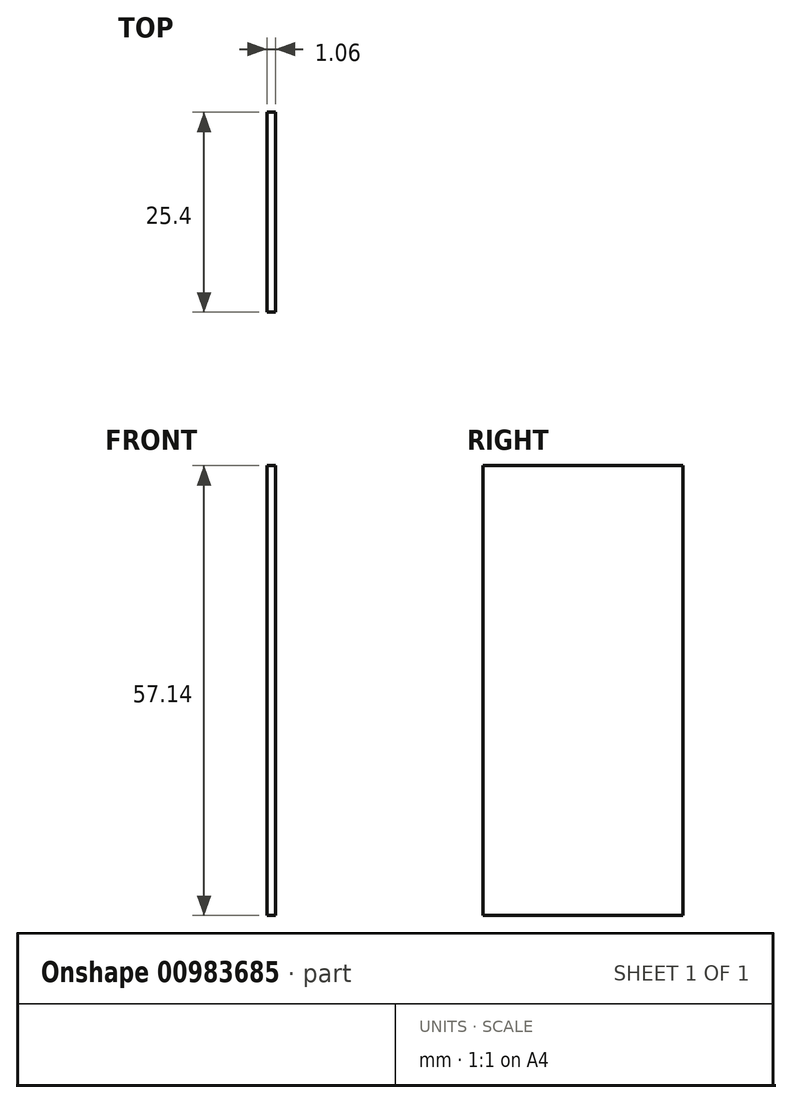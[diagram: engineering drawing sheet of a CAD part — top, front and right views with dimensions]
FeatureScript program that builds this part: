
annotation { "Feature Type Name" : "Feature", "Feature Type Description" : "" }
export const myFeature = defineFeature(function(context is Context, id is Id, definition is map)
    precondition{}
    {
        {
            var Q0;
            Q0=qCreatedBy(makeId("Right.planeOp"),FACE);
            var sketch = newSketch(context, id + "F0", { "sketchPlane" : qUnion([Q0])});
            skLineSegment(sketch, "E0.bottom", {"start": v(12.7, 28.58) * mm, "end": v(-12.7, 28.58) * mm});
            skLineSegment(sketch, "E0.top", {"start": v(12.7, -28.58) * mm, "end": v(-12.7, -28.58) * mm});
            skLineSegment(sketch, "E0.left", {"start": v(12.7, 28.58) * mm, "end": v(12.7, -28.58) * mm});
            skLineSegment(sketch, "E0.right", {"start": v(-12.7, 28.58) * mm, "end": v(-12.7, -28.58) * mm});
            skPoint(sketch, "E0.middle", {"position": v(0, 0) * mm});
            skSolve(sketch);
        }
        {
            var Q0;
            Q0 = qSketchRegion(id + "F0", true);
            extrude(context, id + "F1", {"entities" : qUnion([Q0]), "depth" : 1.06 * mm, "offsetDistance" : 25.4 * mm});
        }
    });
